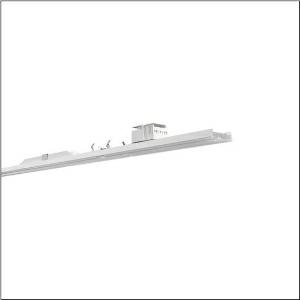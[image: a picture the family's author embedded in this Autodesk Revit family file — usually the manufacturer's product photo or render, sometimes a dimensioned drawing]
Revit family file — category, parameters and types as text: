
# Revit family: licross_r__11_recessed_ho_51tl18dv4m5l_1434
name_source: partatom
category: Lighting Fixtures
units: mm (PartAtom-declared; Revit-internal decimal feet)

## family parameters
Cut with Voids When Loaded = No
Host = Face
Light Source = No
Part Type = Normal
Room Calculation Point = No
Round Connector Dimension = Use Diameter
Shared = No

## types (1)
- --- (1 x LED, 25960 lm, 150.2 W, 4000K)
    Apparent Load = 150 VA
    CIE Flux Codes = 78 94 99 100 100
    Color Rendering = 80
    Color Temperature = 4000K
    Default Elevation = 1800 mm
    Description = Licross® 11 Recessed HOluminaire insert, length: 2.250mm, width: 66mm, height: 67mm, LED rated luminous flux: 25.960lm, light colour: 840, control gear: DALI 2, control gear: ECG DALI, with plug, 5-pole, with phase selection, mains connection: 220..240V, AC, 50/60Hz, halogen-free wiring, primary optical cover: cover, of PMMA, light emission: direct distribution, protection rating (complete): IP40, insulation class (complete): insulation class I (protective earthing), certification: CE, ENEC, VDE, protection symbol: D if used in an environment without relevant dust loads with corresponding accessories, permissible ambient temperature for indoor applications: -35..+35°C, corresponds to IFS (International Featured Standards) requirements for safety and quality in the food industry, reducing of maximum allowable ambient temperature of 5°C with ceiling mounting, packaging unit: 1 piece
    Height = 58 mm
    Lamp = 1 x LED
    Lamp Light Flux = 25960 lm
    Lamp Power = 150.2 W
    Lamp count = 1
    Length = 2250 mm
    Luminous efficacy = 173 lm/W
    Manufacturer = Siteco
    ModVariant = No
    Model = 51TL18DV4M5L
    Mounting Place = Ceiling
    Mounting Type = Pendant
    Number of Poles = 1
    OnlyDefault = Yes
    Power Factor = 1
    Product Name = Licross® 11 Recessed HO
    Product group = luminaire insert
    ProductGroupID = 902
    Protection Class = Protection class I
    Protection Degree = IP 40
    RLX_Detail_Level = 1
    RlxData = <blob elided: 27493 chars, md5=b377a14b>
    Socket = socket
    Standby Power = 0 W
    System Light Flux = 25961 lm
    System Power = 150 W
    Type Comments = factory setting: luminous flux: 100 % | dim-lin: 254 | 575 mA
    Type Image = l_1266722.jpg
    URL = http://relux.com
    VarID = @adj_133162
    Voltage = 0 V
    Weight = 0.00 kg
    Width = 66 mm

## geometry (parser evidence)
native form markers: Blend x4, Sweep x11
no freeform markers — native parametric forms only
